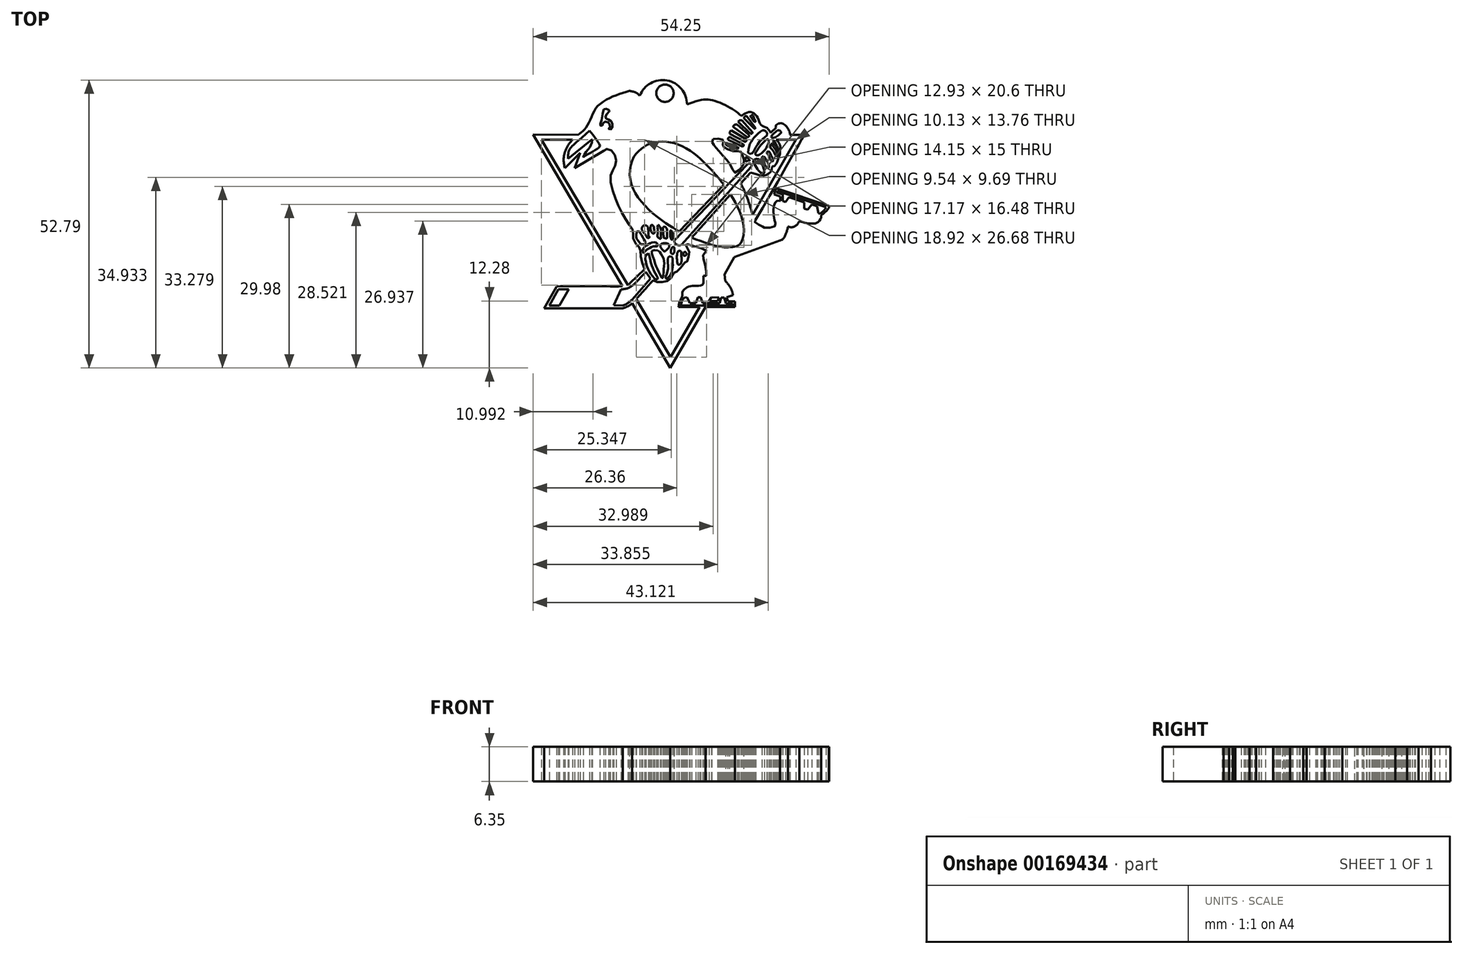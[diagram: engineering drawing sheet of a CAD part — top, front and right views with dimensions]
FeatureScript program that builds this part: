
annotation { "Feature Type Name" : "Feature", "Feature Type Description" : "" }
export const myFeature = defineFeature(function(context is Context, id is Id, definition is map)
    precondition{}
    {
        {
            var Q0;
            Q0=qCreatedBy(makeId("Top.planeOp"),FACE);
            var sketch = newSketch(context, id + "F0", { "sketchPlane" : qUnion([Q0])});
            skFitSpline(sketch, "E0", {"points": [v(-11.66, 22.11) * mm, v(-14.9, 20.96) * mm, v(-17.67, 19.07) * mm, v(-18.96, 16.5) * mm, v(-20.1, 14.81) * mm, v(-20.99, 14.14) * mm, v(-22.68, 12.45) * mm, v(-23.69, 9.95) * mm, v(-23.49, 7.92) * mm], "startDerivative": vector(-21.89, -6.83) * mm, "endDerivative": vector(3.66, -17.18) * mm});
            skLineSegment(sketch, "E1", {"start": v(-23.49, 7.92) * mm, "end": v(-20.66, 10.76) * mm});
            skLineSegment(sketch, "E2", {"start": v(-20.66, 10.76) * mm, "end": v(-21.67, 7.92) * mm});
            skLineSegment(sketch, "E3", {"start": v(-21.67, 7.92) * mm, "end": v(-16.36, 11.12) * mm});
            skFitSpline(sketch, "E4", {"points": [v(-16.36, 11.12) * mm, v(-15.72, 11.45) * mm, v(-14.56, 10.76) * mm, v(-14.11, 9.2) * mm, v(-14.56, 7.79) * mm, v(-15.16, 6.34) * mm, v(-14.4, 2.8) * mm, v(-13.15, 0) * mm, v(-11.62, -2.54) * mm, v(-10.94, -3.62) * mm, v(-10.98, -4.83) * mm, v(-10.14, -6.32) * mm, v(-9.73, -6.76) * mm, v(-9.57, -8.32) * mm, v(-8.85, -10.57) * mm], "startDerivative": vector(12.3, 10.24) * mm, "endDerivative": vector(10.98, -26.47) * mm});
            skLineSegment(sketch, "E5", {"start": v(-8.85, -10.57) * mm, "end": v(-11.54, -13.15) * mm});
            skFitSpline(sketch, "E6", {"points": [v(-11.54, -13.15) * mm, v(-12.04, -13.56) * mm, v(-13.6, -13.74) * mm, v(-17.38, -13.73) * mm, v(-24.98, -13.74) * mm], "startDerivative": vector(-3.45, -3.93) * mm, "endDerivative": vector(-20, -0.1) * mm});
            skLineSegment(sketch, "E7", {"start": v(-24.98, -13.74) * mm, "end": v(-27.28, -17.76) * mm});
            skLineSegment(sketch, "E8", {"start": v(-27.28, -17.76) * mm, "end": v(-12.86, -17.76) * mm});
            skFitSpline(sketch, "E9", {"points": [v(-12.86, -17.76) * mm, v(-11.8, -17.33) * mm, v(-11.18, -16.85) * mm, v(-8.64, -14.12) * mm, v(-7.3, -12.63) * mm], "startDerivative": vector(5.88, 2.24) * mm, "endDerivative": vector(4.25, 4.74) * mm});
            skFitSpline(sketch, "E10", {"points": [v(-7.3, -12.63) * mm, v(-6.48, -12.97) * mm, v(-4.94, -12.87) * mm, v(-4.08, -12.3) * mm, v(-3.24, -11) * mm, v(-2.83, -11) * mm, v(-1.55, -9.39) * mm, v(-1.12, -9.22) * mm, v(-0.79, -8.29) * mm, v(-0.77, -7.12) * mm, v(-1.3, -6.4) * mm, v(-1.28, -6.06) * mm, v(-1.02, -6) * mm, v(0.57, -6.51) * mm, v(2.5, -7.22) * mm, v(2.26, -7.53) * mm, v(1.88, -7.93) * mm, v(1.92, -8.6) * mm, v(2.4, -10.5) * mm, v(2.46, -11.84) * mm], "startDerivative": vector(14.37, -8.4) * mm, "endDerivative": vector(-0.88, -20.05) * mm});
            skLineSegment(sketch, "E11", {"start": v(2.46, -11.84) * mm, "end": v(1.9, -11.84) * mm});
            skLineSegment(sketch, "E12", {"start": v(1.9, -11.84) * mm, "end": v(1.9, -13.06) * mm});
            skFitSpline(sketch, "E13", {"points": [v(1.9, -13.06) * mm, v(1.72, -13.48) * mm, v(0.4, -13.66) * mm, v(-0.65, -13.76) * mm, v(-1.5, -14.21) * mm, v(-1.96, -14.98) * mm, v(-2, -15.7) * mm, v(-2.41, -16.47) * mm, v(-2.64, -17.51) * mm], "startDerivative": vector(-0.54, -5.32) * mm, "endDerivative": vector(-0.93, -8.01) * mm});
            skLineSegment(sketch, "E14", {"start": v(-2.64, -17.51) * mm, "end": v(1.2, -17.51) * mm});
            skLineSegment(sketch, "E15", {"start": v(7.67, -17.51) * mm, "end": v(7.67, -16.5) * mm});
            skLineSegment(sketch, "E16", {"start": v(7.67, -16.5) * mm, "end": v(6.42, -16.5) * mm});
            skLineSegment(sketch, "E17", {"start": v(6.42, -16.5) * mm, "end": v(6.15, -15.76) * mm});
            skLineSegment(sketch, "E18", {"start": v(6.15, -15.76) * mm, "end": v(7.33, -15.33) * mm});
            skFitSpline(sketch, "E19", {"points": [v(5.94, -12.75) * mm, v(6.8, -13.87) * mm, v(7.2, -14.78) * mm, v(7.33, -15.33) * mm], "startDerivative": vector(2.36, -2.75) * mm, "endDerivative": vector(0.37, -2.04) * mm});
            skLineSegment(sketch, "E20", {"start": v(5.94, -12.75) * mm, "end": v(5.77, -11.56) * mm});
            skLineSegment(sketch, "E21", {"start": v(5.77, -11.56) * mm, "end": v(7.59, -8.4) * mm});
            skLineSegment(sketch, "E22", {"start": v(7.59, -8.4) * mm, "end": v(15.97, -5.34) * mm});
            skFitSpline(sketch, "E23", {"points": [v(15.97, -5.34) * mm, v(16.55, -5) * mm, v(17.2, -3.7) * mm, v(17.43, -2.78) * mm], "startDerivative": vector(2.2, 0.72) * mm, "endDerivative": vector(0.57, 2.59) * mm});
            skFitSpline(sketch, "E24", {"points": [v(17.43, -2.78) * mm, v(18.03, -2.9) * mm, v(18.95, -2.57) * mm, v(19.48, -1.77) * mm], "startDerivative": vector(1.93, -0.7) * mm, "endDerivative": vector(1.16, 2.48) * mm});
            skFitSpline(sketch, "E25", {"points": [v(19.48, -1.77) * mm, v(20.71, -2.12) * mm, v(22.16, -2.24) * mm, v(23.03, -1.88) * mm, v(23.5, -1.05) * mm, v(23.53, -0.73) * mm, v(24.07, -0.3) * mm, v(24.92, 0.7) * mm, v(24.92, 1.03) * mm], "startDerivative": vector(7.7, -2.57) * mm, "endDerivative": vector(-0.98, 3.68) * mm});
            skLineSegment(sketch, "E26", {"start": v(24.92, 1.03) * mm, "end": v(15.23, 4.27) * mm});
            skLineSegment(sketch, "E27", {"start": v(15.23, 4.27) * mm, "end": v(14.85, 3.14) * mm});
            skLineSegment(sketch, "E28", {"start": v(14.85, 3.14) * mm, "end": v(16, 2.76) * mm});
            skLineSegment(sketch, "E29", {"start": v(16, 2.76) * mm, "end": v(16, 1.94) * mm});
            skFitSpline(sketch, "E30", {"points": [v(16, 1.94) * mm, v(15.39, 1.94) * mm, v(14.95, 1.39) * mm, v(14.78, 0.23) * mm, v(14.91, -1.48) * mm, v(15.12, -2.23) * mm, v(14.9, -2.78) * mm, v(12.96, -2.97) * mm, v(12.79, -2.76) * mm, v(11.44, -2.08) * mm, v(11.38, -1.78) * mm, v(11.88, -0.89) * mm, v(18.93, 11.42) * mm, v(20.41, 14.02) * mm], "startDerivative": vector(-13.15, 2.37) * mm, "endDerivative": vector(9.12, 16.03) * mm});
            skLineSegment(sketch, "E31", {"start": v(20.41, 14.02) * mm, "end": v(17.76, 14.02) * mm});
            skFitSpline(sketch, "E32", {"points": [v(17.76, 14.02) * mm, v(17.76, 14.4) * mm, v(17.42, 15.21) * mm, v(16.81, 15.91) * mm, v(15.92, 16.16) * mm, v(15.2, 15.76) * mm, v(15.28, 15.38) * mm], "startDerivative": vector(0.33, 2.79) * mm, "endDerivative": vector(1.56, -3.07) * mm});
            skLineSegment(sketch, "E33", {"start": v(15.28, 15.38) * mm, "end": v(14.21, 14.41) * mm});
            skFitSpline(sketch, "E34", {"points": [v(14.21, 14.41) * mm, v(13.97, 14.9) * mm, v(13.28, 15.46) * mm, v(12.49, 15.84) * mm, v(12.01, 16.8) * mm, v(11.4, 17.8) * mm, v(10.53, 18.23) * mm, v(9.53, 17.96) * mm, v(8.83, 17.5) * mm], "startDerivative": vector(-1.92, 5.07) * mm, "endDerivative": vector(-5.43, -3.96) * mm});
            skFitSpline(sketch, "E35", {"points": [v(8.83, 17.5) * mm, v(7.6, 18.51) * mm, v(5.57, 19.67) * mm, v(3.3, 20.44) * mm, v(1.68, 20.48) * mm, v(-1.1, 19.61) * mm, v(-3.76, 18.45) * mm, v(-5.13, 17.88) * mm, v(-6.27, 17.92) * mm, v(-7.23, 18.59) * mm, v(-8.33, 19.82) * mm, v(-9.76, 21.22) * mm, v(-10.44, 21.77) * mm, v(-11.66, 22.11) * mm], "startDerivative": vector(-15.54, 13.66) * mm, "endDerivative": vector(-20.69, 4.2) * mm});
            skLineSegment(sketch, "E36", {"start": v(-29.3, 14.07) * mm, "end": v(-21.08, 14.06) * mm});
            skLineSegment(sketch, "E37", {"start": v(-29.3, 14.07) * mm, "end": v(-12.95, -13.73) * mm});
            skLineSegment(sketch, "E38", {"start": v(-4.14, -28.69) * mm, "end": v(2.3, -17.51) * mm});
            skLineSegment(sketch, "E39.trimOffspring", {"start": v(-11.13, -16.81) * mm, "end": v(-4.14, -28.69) * mm});
            skLineSegment(sketch, "E40.trimOffspring", {"start": v(17.76, 14.02) * mm, "end": v(20.41, 14.02) * mm});
            skFitSpline(sketch, "E41", {"points": [v(-16.34, 18.75) * mm, v(-15.96, 18.83) * mm, v(-15.37, 18.58) * mm, v(-15.27, 18.43) * mm, v(-15.9, 17.73) * mm, v(-16.07, 17.29) * mm, v(-15.91, 17.02) * mm, v(-15.32, 16.78) * mm, v(-14.83, 16.3) * mm, v(-14.75, 15.48) * mm, v(-14.94, 15.1) * mm, v(-15.45, 15.1) * mm, v(-15.26, 15.42) * mm, v(-15.24, 15.92) * mm, v(-15.53, 16.28) * mm, v(-16.06, 16.46) * mm, v(-16.5, 16.1) * mm, v(-16.65, 15.76) * mm, v(-16.92, 15.72) * mm, v(-17.04, 15.79) * mm, v(-16.79, 16.52) * mm, v(-16.34, 18.75) * mm]});
            skFitSpline(sketch, "E42", {"points": [v(-18.97, 14.78) * mm, v(-18.16, 13.83) * mm, v(-17.36, 12.66) * mm, v(-17.06, 12.02) * mm, v(-17.54, 11.5) * mm, v(-18.6, 10.83) * mm, v(-19.76, 10.2) * mm, v(-20.14, 9.97) * mm, v(-19.6, 10.9) * mm, v(-18.75, 12.07) * mm, v(-18.45, 13.25) * mm], "startDerivative": vector(7.53, -8.27) * mm, "endDerivative": vector(1.8, 11.44) * mm});
            skLineSegment(sketch, "E43", {"start": v(-18.45, 13.25) * mm, "end": v(-22.88, 9.68) * mm});
            skFitSpline(sketch, "E44", {"points": [v(-22.88, 9.68) * mm, v(-22.88, 10.5) * mm, v(-22.53, 11.53) * mm, v(-21.24, 12.8) * mm, v(-19.48, 14.34) * mm, v(-18.97, 14.78) * mm], "startDerivative": vector(-0.3, 5.01) * mm, "endDerivative": vector(2.91, 2.54) * mm});
            skFitSpline(sketch, "E45", {"points": [v(-9.48, 11.5) * mm, v(-10.86, 9.95) * mm, v(-11.58, 6.7) * mm, v(-10.56, 3.36) * mm, v(-7.73, 0) * mm, v(-4.36, -2.57) * mm, v(-2.55, -3.65) * mm], "startDerivative": vector(-11.26, -9.73) * mm, "endDerivative": vector(12.34, -7.02) * mm});
            skFitSpline(sketch, "E46", {"points": [v(-0.21, -4.8) * mm, v(1.43, -5.46) * mm, v(3.63, -6.2) * mm, v(5.55, -6.57) * mm, v(7.2, -6.58) * mm, v(8.28, -6.26) * mm, v(8.89, -5.64) * mm, v(9.28, -4.39) * mm, v(9.28, -2.5) * mm, v(8.68, -0.29) * mm, v(7.81, 1.57) * mm, v(6.89, 3.1) * mm], "startDerivative": vector(16.89, -6.96) * mm, "endDerivative": vector(-10.12, 15.9) * mm});
            skFitSpline(sketch, "E47", {"points": [v(5.65, 4.88) * mm, v(4.52, 6.36) * mm, v(2, 9) * mm, v(0.52, 10.38) * mm, v(-1.43, 11.65) * mm, v(-3.22, 12.43) * mm, v(-5, 12.8) * mm, v(-6.7, 12.74) * mm, v(-8.4, 12.18) * mm, v(-9.48, 11.5) * mm], "startDerivative": vector(-8.79, 12.61) * mm, "endDerivative": vector(-11.17, -8.03) * mm});
            skLineSegment(sketch, "E48", {"start": v(-2.55, -3.65) * mm, "end": v(5.65, 4.88) * mm});
            skLineSegment(sketch, "E49", {"start": v(6.89, 3.1) * mm, "end": v(-0.21, -4.8) * mm});
            skFitSpline(sketch, "E50", {"points": [v(10.7, 17.62) * mm, v(10.56, 17.44) * mm, v(10.86, 16.97) * mm, v(11.16, 16.54) * mm, v(11.47, 16.46) * mm, v(11.3, 16.9) * mm, v(10.95, 17.6) * mm, v(10.7, 17.62) * mm]});
            skLineSegment(sketch, "E51", {"start": v(9.83, 17.49) * mm, "end": v(11.44, 15.33) * mm});
            skLineSegment(sketch, "E52", {"start": v(9.36, 17.12) * mm, "end": v(11.16, 15.24) * mm});
            skLineSegment(sketch, "E53", {"start": v(8.99, 16.7) * mm, "end": v(10.95, 14.48) * mm});
            skLineSegment(sketch, "E54", {"start": v(8.3, 16.46) * mm, "end": v(10.49, 14.28) * mm});
            skLineSegment(sketch, "E55", {"start": v(8.06, 15.92) * mm, "end": v(10.2, 14.1) * mm});
            skLineSegment(sketch, "E56", {"start": v(7.36, 15.51) * mm, "end": v(10.02, 13.6) * mm});
            skLineSegment(sketch, "E57", {"start": v(6.97, 14.85) * mm, "end": v(9.78, 13.21) * mm});
            skLineSegment(sketch, "E58", {"start": v(6.76, 14.21) * mm, "end": v(9.54, 12.76) * mm});
            skLineSegment(sketch, "E59", {"start": v(6.65, 13.64) * mm, "end": v(9.29, 12.29) * mm});
            skLineSegment(sketch, "E60", {"start": v(6.45, 13.15) * mm, "end": v(9.1, 11.9) * mm});
            skLineSegment(sketch, "E61", {"start": v(6.13, 12.6) * mm, "end": v(8.44, 11.64) * mm});
            skFitSpline(sketch, "E62", {"points": [v(6.13, 12.6) * mm, v(6.05, 12.35) * mm, v(6.33, 12.05) * mm, v(7.06, 11.71) * mm, v(8.03, 11.58) * mm, v(8.44, 11.64) * mm], "startDerivative": vector(-1.05, -1.86) * mm, "endDerivative": vector(2.07, 0.5) * mm});
            skFitSpline(sketch, "E63", {"points": [v(6.65, 13.64) * mm, v(6.46, 13.41) * mm, v(6.45, 13.15) * mm], "startDerivative": vector(-0.48, -0.41) * mm, "endDerivative": vector(0.08, -0.57) * mm});
            skFitSpline(sketch, "E64", {"points": [v(9.29, 12.29) * mm, v(9.29, 12.03) * mm, v(9.1, 11.9) * mm], "startDerivative": vector(0.1, -0.56) * mm, "endDerivative": vector(-0.48, -0.21) * mm});
            skFitSpline(sketch, "E65", {"points": [v(6.97, 14.85) * mm, v(6.78, 14.59) * mm, v(6.76, 14.21) * mm], "startDerivative": vector(-0.5, -0.5) * mm, "endDerivative": vector(0.05, -0.77) * mm});
            skFitSpline(sketch, "E66", {"points": [v(9.78, 13.21) * mm, v(9.78, 12.92) * mm, v(9.54, 12.76) * mm], "startDerivative": vector(0.12, -0.66) * mm, "endDerivative": vector(-0.6, -0.26) * mm});
            skFitSpline(sketch, "E67", {"points": [v(7.36, 15.51) * mm, v(7.57, 15.85) * mm, v(8.06, 15.92) * mm], "startDerivative": vector(0.31, 0.85) * mm, "endDerivative": vector(1.06, -0.02) * mm});
            skFitSpline(sketch, "E68", {"points": [v(10.2, 14.1) * mm, v(10.29, 13.8) * mm, v(10.02, 13.6) * mm], "startDerivative": vector(0.35, -0.64) * mm, "endDerivative": vector(-0.7, -0.35) * mm});
            skFitSpline(sketch, "E69", {"points": [v(8.3, 16.46) * mm, v(8.58, 16.7) * mm, v(8.99, 16.7) * mm], "startDerivative": vector(0.54, 0.6) * mm, "endDerivative": vector(0.85, -0.12) * mm});
            skFitSpline(sketch, "E70", {"points": [v(10.49, 14.28) * mm, v(10.8, 14.28) * mm, v(10.95, 14.48) * mm], "startDerivative": vector(0.66, -0.11) * mm, "endDerivative": vector(0.24, 0.53) * mm});
            skFitSpline(sketch, "E71", {"points": [v(11.16, 15.24) * mm, v(11.37, 15.18) * mm, v(11.44, 15.33) * mm], "startDerivative": vector(0.44, -0.24) * mm, "endDerivative": vector(0.1, 0.43) * mm});
            skFitSpline(sketch, "E72", {"points": [v(9.36, 17.12) * mm, v(9.5, 17.42) * mm, v(9.83, 17.49) * mm], "startDerivative": vector(0.2, 0.72) * mm, "endDerivative": vector(0.74, 0.03) * mm});
            skFitSpline(sketch, "E73", {"points": [v(12.7, 14.85) * mm, v(12.16, 14.48) * mm, v(11.62, 13.98) * mm, v(11.16, 13.52) * mm, v(10.75, 12.9) * mm, v(10.4, 12.29) * mm, v(10.2, 11.51) * mm, v(10.13, 10.74) * mm, v(10.74, 10.6) * mm, v(11.16, 11.08) * mm, v(11.9, 12.35) * mm, v(12.57, 13.15) * mm, v(13.47, 13.83) * mm, v(13.6, 14.1) * mm, v(13.47, 14.6) * mm, v(13.05, 14.85) * mm, v(12.7, 14.85) * mm]});
            skFitSpline(sketch, "E74", {"points": [v(13.52, 13.21) * mm, v(13.1, 12.87) * mm, v(12.55, 12.29) * mm, v(12.04, 11.64) * mm, v(11.6, 10.92) * mm, v(11.44, 10.55) * mm, v(11.62, 10.32) * mm, v(11.97, 10.33) * mm, v(12.63, 10.7) * mm, v(13.38, 11.56) * mm, v(13.74, 12.29) * mm, v(13.92, 12.97) * mm, v(13.7, 13.21) * mm, v(13.52, 13.21) * mm]});
            skFitSpline(sketch, "E75", {"points": [v(15.48, 14.85) * mm, v(14.9, 14.38) * mm, v(14.41, 13.83) * mm, v(14.4, 13.53) * mm, v(14.87, 13.5) * mm, v(15.53, 13.85) * mm, v(15.97, 14.21) * mm, v(16.17, 14.48) * mm, v(16.04, 14.73) * mm, v(15.75, 14.85) * mm, v(15.48, 14.85) * mm]});
            skFitSpline(sketch, "E76", {"points": [v(-8.6, -11.1) * mm, v(-7.81, -12.31) * mm], "startDerivative": vector(0.79, -1.22) * mm, "endDerivative": vector(0.79, -1.22) * mm});
            skLineSegment(sketch, "E77", {"start": v(-8.6, -11.1) * mm, "end": v(-10.92, -13.44) * mm});
            skLineSegment(sketch, "E78", {"start": v(-7.81, -12.31) * mm, "end": v(-11.11, -16.11) * mm});
            skFitSpline(sketch, "E79", {"points": [v(-11.11, -16.11) * mm, v(-11.54, -16.52) * mm, v(-12.37, -17.07) * mm, v(-12.86, -17.24) * mm], "startDerivative": vector(-1.2, -1.25) * mm, "endDerivative": vector(-1.57, -0.42) * mm});
            skFitSpline(sketch, "E80", {"points": [v(-10.92, -13.44) * mm, v(-11.7, -13.98) * mm, v(-12.52, -14.22) * mm, v(-13.19, -14.26) * mm], "startDerivative": vector(-2.1, -1.7) * mm, "endDerivative": vector(-2.16, -0.04) * mm});
            skLineSegment(sketch, "E81", {"start": v(-13.19, -14.26) * mm, "end": v(-14.55, -17.21) * mm});
            skLineSegment(sketch, "E82", {"start": v(-14.55, -17.21) * mm, "end": v(-12.86, -17.24) * mm});
            skLineSegment(sketch, "E83", {"start": v(-24.7, -14.26) * mm, "end": v(-22.8, -14.26) * mm});
            skLineSegment(sketch, "E84", {"start": v(-22.8, -14.26) * mm, "end": v(-24.5, -17.25) * mm});
            skLineSegment(sketch, "E85", {"start": v(-24.5, -17.25) * mm, "end": v(-26.31, -17.25) * mm});
            skLineSegment(sketch, "E86", {"start": v(-26.31, -17.25) * mm, "end": v(-24.7, -14.26) * mm});
            skLineSegment(sketch, "E87", {"start": v(-2.15, -17.24) * mm, "end": v(7.25, -17.24) * mm});
            skLineSegment(sketch, "E88", {"start": v(7.25, -17.24) * mm, "end": v(7.25, -16.9) * mm});
            skLineSegment(sketch, "E89", {"start": v(7.25, -16.9) * mm, "end": v(6.06, -16.9) * mm});
            skLineSegment(sketch, "E90", {"start": v(6.06, -16.9) * mm, "end": v(5.71, -15.78) * mm});
            skLineSegment(sketch, "E91", {"start": v(5.71, -15.78) * mm, "end": v(5.18, -15.78) * mm});
            skLineSegment(sketch, "E92", {"start": v(5.18, -15.78) * mm, "end": v(4.88, -16.83) * mm});
            skLineSegment(sketch, "E93", {"start": v(4.88, -16.83) * mm, "end": v(1.82, -16.83) * mm});
            skLineSegment(sketch, "E94", {"start": v(1.82, -16.83) * mm, "end": v(1.43, -15.75) * mm});
            skLineSegment(sketch, "E95", {"start": v(1.43, -15.75) * mm, "end": v(0.88, -15.75) * mm});
            skLineSegment(sketch, "E96", {"start": v(0.88, -15.75) * mm, "end": v(0.52, -16.83) * mm});
            skLineSegment(sketch, "E97", {"start": v(0.52, -16.83) * mm, "end": v(-0.55, -16.83) * mm});
            skLineSegment(sketch, "E98", {"start": v(-0.55, -16.83) * mm, "end": v(-1.11, -15.77) * mm});
            skLineSegment(sketch, "E99", {"start": v(-1.11, -15.77) * mm, "end": v(-1.53, -15.78) * mm});
            skFitSpline(sketch, "E100", {"points": [v(-1.53, -15.78) * mm, v(-2, -16.38) * mm, v(-2.15, -17.24) * mm], "startDerivative": vector(-1.14, -1.15) * mm, "endDerivative": vector(-0.1, -1.77) * mm});
            skLineSegment(sketch, "E101", {"start": v(3.38, -15.74) * mm, "end": v(2.95, -16.46) * mm});
            skLineSegment(sketch, "E102", {"start": v(2.95, -16.46) * mm, "end": v(4.56, -16.46) * mm});
            skLineSegment(sketch, "E103", {"start": v(4.56, -16.46) * mm, "end": v(4.78, -15.8) * mm});
            skLineSegment(sketch, "E104", {"start": v(4.78, -15.8) * mm, "end": v(3.38, -15.74) * mm});
            skFitSpline(sketch, "E105", {"points": [v(-3.38, -5.36) * mm, v(-3.3, -5.8) * mm, v(-2.63, -6.2) * mm, v(-2.07, -6.1) * mm], "startDerivative": vector(-0.09, -1.53) * mm, "endDerivative": vector(1.59, 0.63) * mm});
            skLineSegment(sketch, "E106", {"start": v(-3.38, -5.36) * mm, "end": v(10, 8.67) * mm});
            skLineSegment(sketch, "E107", {"start": v(-2.07, -6.1) * mm, "end": v(10.64, 8.13) * mm});
            skFitSpline(sketch, "E108", {"points": [v(10, 8.67) * mm, v(10.34, 8.79) * mm, v(10.64, 8.67) * mm, v(10.76, 8.38) * mm, v(10.64, 8.13) * mm], "startDerivative": vector(1.29, 0.65) * mm, "endDerivative": vector(-0.73, -1.04) * mm});
            skLineSegment(sketch, "E109", {"start": v(15.44, 3.75) * mm, "end": v(24.4, 0.75) * mm});
            skLineSegment(sketch, "E110", {"start": v(15.44, 3.75) * mm, "end": v(15.34, 3.48) * mm});
            skLineSegment(sketch, "E111", {"start": v(15.34, 3.48) * mm, "end": v(16.46, 3.1) * mm});
            skLineSegment(sketch, "E112", {"start": v(16.46, 3.1) * mm, "end": v(16.46, 1.91) * mm});
            skLineSegment(sketch, "E113", {"start": v(16.46, 1.91) * mm, "end": v(16.96, 1.74) * mm});
            skLineSegment(sketch, "E114", {"start": v(16.96, 1.74) * mm, "end": v(17.59, 2.62) * mm});
            skLineSegment(sketch, "E115", {"start": v(17.59, 2.62) * mm, "end": v(20.42, 1.67) * mm});
            skLineSegment(sketch, "E116", {"start": v(20.42, 1.67) * mm, "end": v(20.42, 0.53) * mm});
            skLineSegment(sketch, "E117", {"start": v(20.42, 0.53) * mm, "end": v(21.02, 0.32) * mm});
            skLineSegment(sketch, "E118", {"start": v(21.02, 0.32) * mm, "end": v(21.77, 1.27) * mm});
            skLineSegment(sketch, "E119", {"start": v(21.77, 1.27) * mm, "end": v(22.74, 0.94) * mm});
            skLineSegment(sketch, "E120", {"start": v(22.74, 0.94) * mm, "end": v(23, -0.3) * mm});
            skLineSegment(sketch, "E121", {"start": v(23, -0.3) * mm, "end": v(23.35, -0.42) * mm});
            skFitSpline(sketch, "E122", {"points": [v(23.35, -0.42) * mm, v(24.1, 0.26) * mm, v(24.4, 0.75) * mm], "startDerivative": vector(1.48, 1.2) * mm, "endDerivative": vector(0.57, 1.14) * mm});
            skFitSpline(sketch, "E123", {"points": [v(-10.1, -3.56) * mm, v(-10.36, -4.09) * mm, v(-10.38, -4.85) * mm, v(-9.7, -5.87) * mm, v(-9.52, -6.04) * mm, v(-8.97, -6) * mm, v(-8.7, -5.81) * mm, v(-9.12, -4.89) * mm, v(-10.1, -3.56) * mm]});
            skFitSpline(sketch, "E124", {"points": [v(-9.09, -2.63) * mm, v(-9.37, -3.12) * mm, v(-9.2, -3.67) * mm, v(-8.76, -4.22) * mm, v(-8.42, -4.8) * mm, v(-8.18, -4.89) * mm, v(-7.97, -4.7) * mm, v(-8.14, -4.41) * mm, v(-8.2, -3.65) * mm, v(-8.25, -2.97) * mm, v(-8.5, -2.6) * mm, v(-9.09, -2.63) * mm]});
            skFitSpline(sketch, "E125", {"points": [v(-7.59, -2.46) * mm, v(-7.78, -2.97) * mm, v(-7.63, -3.77) * mm, v(-7.2, -4.07) * mm, v(-7.06, -3.9) * mm, v(-7.13, -3.27) * mm, v(-7.2, -2.76) * mm, v(-7.59, -2.46) * mm]});
            skFitSpline(sketch, "E126", {"points": [v(-6.4, -2.48) * mm, v(-6.49, -3.25) * mm, v(-6.49, -4.18) * mm, v(-6.47, -4.71) * mm, v(-5.96, -5.02) * mm, v(-5.88, -4.62) * mm, v(-5.86, -3.63) * mm, v(-5.94, -2.99) * mm, v(-6.4, -2.48) * mm]});
            skFitSpline(sketch, "E127", {"points": [v(-5.44, -2.84) * mm, v(-5.48, -3.73) * mm, v(-5.4, -4.58) * mm, v(-5.31, -4.85) * mm, v(-4.84, -4.94) * mm, v(-4.72, -4.75) * mm, v(-4.76, -4.03) * mm, v(-4.76, -3.25) * mm, v(-5.03, -2.91) * mm, v(-5.44, -2.84) * mm]});
            skFitSpline(sketch, "E128", {"points": [v(-4.12, -3.48) * mm, v(-4.2, -4.22) * mm, v(-4.1, -4.8) * mm, v(-3.9, -5.23) * mm, v(-3.76, -5.08) * mm, v(-3.72, -4.35) * mm, v(-3.8, -3.8) * mm, v(-4.12, -3.48) * mm]});
            skFitSpline(sketch, "E129", {"points": [v(-9.22, -7) * mm, v(-8.61, -6.33) * mm, v(-7.74, -5.78) * mm, v(-6.77, -5.7) * mm, v(-6.54, -6.04) * mm, v(-6.6, -6.4) * mm, v(-7.13, -6.38) * mm, v(-7.95, -6.74) * mm, v(-8.57, -7.1) * mm, v(-9.12, -7.58) * mm, v(-9.22, -7) * mm]});
            skFitSpline(sketch, "E130", {"points": [v(-5.43, -5.81) * mm, v(-5.96, -6.14) * mm, v(-5.94, -6.54) * mm, v(-5.56, -7.07) * mm, v(-5.24, -7.35) * mm, v(-4.82, -7.07) * mm, v(-4.44, -6.67) * mm, v(-4.36, -6.27) * mm, v(-4.57, -5.9) * mm, v(-5.43, -5.81) * mm]});
            skFitSpline(sketch, "E131", {"points": [v(-3.78, -6.6) * mm, v(-4, -6.97) * mm, v(-4.02, -7.56) * mm, v(-3.76, -7.82) * mm, v(-3.43, -7.48) * mm, v(-3.42, -6.97) * mm, v(-3.47, -6.6) * mm, v(-3.78, -6.6) * mm]});
            skFitSpline(sketch, "E132", {"points": [v(-2.64, -7.24) * mm, v(-2.92, -7.94) * mm, v(-2.92, -9.02) * mm, v(-2.7, -9.78) * mm, v(-2.24, -9.59) * mm, v(-2.09, -8.87) * mm, v(-2.13, -7.92) * mm, v(-2.18, -7.33) * mm, v(-2.64, -7.24) * mm]});
            skFitSpline(sketch, "E133", {"points": [v(-1.58, -7.43) * mm, v(-1.75, -8.05) * mm, v(-1.39, -8.1) * mm, v(-1.2, -7.77) * mm, v(-1.58, -7.43) * mm]});
            skFitSpline(sketch, "E134", {"points": [v(-8.27, -7.7) * mm, v(-7.76, -9.15) * mm, v(-7.3, -10.56) * mm, v(-6.77, -11.66) * mm, v(-6.43, -12.32) * mm, v(-6.77, -12.49) * mm, v(-7.25, -12.1) * mm, v(-7.93, -11.14) * mm, v(-8.48, -9.99) * mm, v(-8.65, -9.11) * mm, v(-8.74, -8.36) * mm, v(-8.27, -7.7) * mm]});
            skFitSpline(sketch, "E135", {"points": [v(-7.53, -7.26) * mm, v(-7.27, -8.56) * mm, v(-6.83, -9.91) * mm, v(-6.2, -11.18) * mm, v(-5.6, -12.26) * mm, v(-5.44, -11.73) * mm, v(-5.35, -10.56) * mm, v(-5.27, -9.36) * mm, v(-5.43, -8.6) * mm, v(-5.9, -7.7) * mm, v(-6.43, -7.22) * mm, v(-7.53, -7.26) * mm]});
            skFitSpline(sketch, "E136", {"points": [v(-4.55, -8.41) * mm, v(-4.17, -8.22) * mm, v(-3.8, -8.47) * mm, v(-3.72, -9.11) * mm, v(-3.68, -9.82) * mm, v(-3.74, -10.46) * mm, v(-3.93, -11.14) * mm, v(-4.34, -11.86) * mm, v(-4.6, -12.22) * mm, v(-4.61, -12.41) * mm, v(-4.84, -12.38) * mm, v(-4.99, -12.19) * mm, v(-4.88, -11.64) * mm, v(-4.55, -10.6) * mm, v(-4.61, -9.34) * mm, v(-4.55, -8.41) * mm]});
            skFitSpline(sketch, "E137", {"points": [v(9.72, 9.15) * mm, v(10.02, 9.3) * mm, v(10.38, 9.34) * mm, v(10.17, 9.7) * mm, v(9.73, 9.95) * mm, v(9.63, 9.56) * mm, v(9.72, 9.15) * mm]});
            skFitSpline(sketch, "E138", {"points": [v(11.07, 9.34) * mm, v(11.39, 8.48) * mm, v(11.95, 7.53) * mm, v(12.44, 7.1) * mm, v(12.96, 6.89) * mm, v(13.05, 7.62) * mm, v(12.83, 8.22) * mm, v(12.49, 9.03) * mm, v(12, 9.63) * mm, v(11.07, 9.34) * mm]});
            skFitSpline(sketch, "E139", {"points": [v(12.67, 10.05) * mm, v(12.77, 9.64) * mm, v(13.01, 9.02) * mm, v(13.43, 8.19) * mm, v(13.82, 8) * mm, v(13.92, 8.3) * mm, v(13.74, 8.88) * mm, v(13.35, 9.6) * mm, v(13.15, 9.95) * mm, v(12.67, 10.05) * mm]});
            skFitSpline(sketch, "E140", {"points": [v(13.54, 10.8) * mm, v(13.86, 10.27) * mm, v(14.08, 9.68) * mm, v(14.41, 9.3) * mm, v(14.65, 9.19) * mm, v(14.62, 9.73) * mm, v(14.33, 10.28) * mm, v(13.89, 10.98) * mm, v(13.54, 10.8) * mm]});
            skFitSpline(sketch, "E141", {"points": [v(14.16, 11.82) * mm, v(14.41, 12.41) * mm, v(14.8, 11.79) * mm, v(15.3, 11.06) * mm, v(15.53, 10.39) * mm, v(15.58, 10.15) * mm, v(15.34, 10.12) * mm, v(14.9, 10.76) * mm, v(14.38, 11.5) * mm, v(14.16, 11.82) * mm]});
            skFitSpline(sketch, "E142", {"points": [v(14.7, 12.82) * mm, v(15.2, 12) * mm, v(15.53, 11.23) * mm, v(15.68, 11) * mm, v(15.55, 11.69) * mm, v(15.2, 12.43) * mm, v(14.84, 12.99) * mm, v(14.7, 12.82) * mm]});
            skLineSegment(sketch, "E143", {"start": v(18.88, 13.12) * mm, "end": v(10.94, -0.64) * mm});
            skLineSegment(sketch, "E144", {"start": v(-4.1, -26.7) * mm, "end": v(-10.42, -16.07) * mm});
            skLineSegment(sketch, "E145.trimOffspring", {"start": v(-18.56, 13.16) * mm, "end": v(-18.46, 13.16) * mm});
            skLineSegment(sketch, "E146", {"start": v(-27.77, 13.17) * mm, "end": v(-22.07, 13.17) * mm});
            skLineSegment(sketch, "E147.trimOffspring", {"start": v(15.28, 13.12) * mm, "end": v(18.88, 13.12) * mm});
            skFitSpline(sketch, "E148", {"points": [v(15.28, 13.12) * mm, v(15.75, 12.62) * mm, v(16.02, 11.75) * mm, v(15.97, 10.92) * mm, v(15.9, 10.24) * mm, v(15.73, 9.95) * mm, v(15.5, 9.25) * mm, v(15.21, 8.67) * mm, v(14.74, 8.24) * mm, v(14.55, 8.3) * mm, v(14.44, 7.55) * mm, v(13.99, 7.04) * mm, v(13.18, 6.59) * mm, v(11.8, 6.75) * mm, v(10.53, 7.15) * mm], "startDerivative": vector(7.19, -6.43) * mm, "endDerivative": vector(-12.76, 4.2) * mm});
            skLineSegment(sketch, "E149", {"start": v(10.53, 7.15) * mm, "end": v(8.76, 5.17) * mm});
            skFitSpline(sketch, "E150", {"points": [v(8.76, 5.17) * mm, v(9.42, 3.8) * mm, v(10.14, 1.97) * mm, v(10.8, -0.1) * mm, v(10.94, -0.64) * mm], "startDerivative": vector(2.62, -5.3) * mm, "endDerivative": vector(0.7, -2.86) * mm});
            skLineSegment(sketch, "E151.trimOffspring", {"start": v(1.2, -17.51) * mm, "end": v(-4.1, -26.7) * mm});
            skLineSegment(sketch, "E152.trimOffspring", {"start": v(-11.94, -13.5) * mm, "end": v(-27.77, 13.17) * mm});
            skFitSpline(sketch, "E153", {"points": [v(3.68, 13.25) * mm, v(5.3, 13.2) * mm, v(5.6, 12.94) * mm, v(5.44, 12.33) * mm, v(5.6, 11.9) * mm, v(6.43, 11.34) * mm, v(8.08, 11.02) * mm, v(8.78, 10.98) * mm, v(9.18, 9.85) * mm, v(9.32, 8.77) * mm, v(7.72, 7.1) * mm, v(7.06, 8.2) * mm, v(5.76, 9.92) * mm, v(4.5, 11.4) * mm, v(3.88, 12.1) * mm, v(3.5, 12.69) * mm, v(3.68, 13.25) * mm]});
            skArc(sketch, "E154", {"start": v(-1.1, 19.61) * mm, "mid": v(-4.75, 24.02) * mm, "end": v(-9.76, 21.22) * mm});
            skCircle(sketch, "E155", {"center": v(-5.13, 21.68) * mm, "radius": 1.59 * mm});
            skLineSegment(sketch, "E156.trimOffspring", {"start": v(2.3, -17.51) * mm, "end": v(7.67, -17.51) * mm});
            skSolve(sketch);
        }
        {
            var Q0;
            {var subQ17=sQuery(id+"F0.wireOp",EDGE,"E1");Q0=makeQuery(id+"F0.imprint","IMPRINT",FACE,{"disambiguationData":[TD([[makeQuery(id+"F0.imprint","IMPRINT",EDGE,{"derivedFrom":subQ17}),1.0]])]});}
            var Q1;
            {var subQ0=sQuery(id+"F0.wireOp",EDGE,"E36");Q1=makeQuery(id+"F0.imprint","IMPRINT",FACE,{"disambiguationData":[TD([[makeQuery(id+"F0.imprint","IMPRINT",EDGE,{"derivedFrom":subQ0}),-1.0]])]});}
            var Q2;
            {var subQ3=sQuery(id+"F0.wireOp",EDGE,"E38");Q2=makeQuery(id+"F0.imprint","IMPRINT",FACE,{"disambiguationData":[TD([[makeQuery(id+"F0.imprint","IMPRINT",EDGE,{"derivedFrom":subQ3}),1.0]])]});}
            var Q3;
            {var subQ0=sQuery(id+"F0.wireOp",EDGE,"E154");Q3=makeQuery(id+"F0.imprint","IMPRINT",FACE,{"disambiguationData":[TD([[makeQuery(id+"F0.imprint","IMPRINT",EDGE,{"derivedFrom":subQ0}),1.0]])]});}
            extrude(context, id + "F1", {"entities" : qUnion([Q0, Q1, Q2, Q3]), "depth" : 6.35 * mm});
        }
    });
